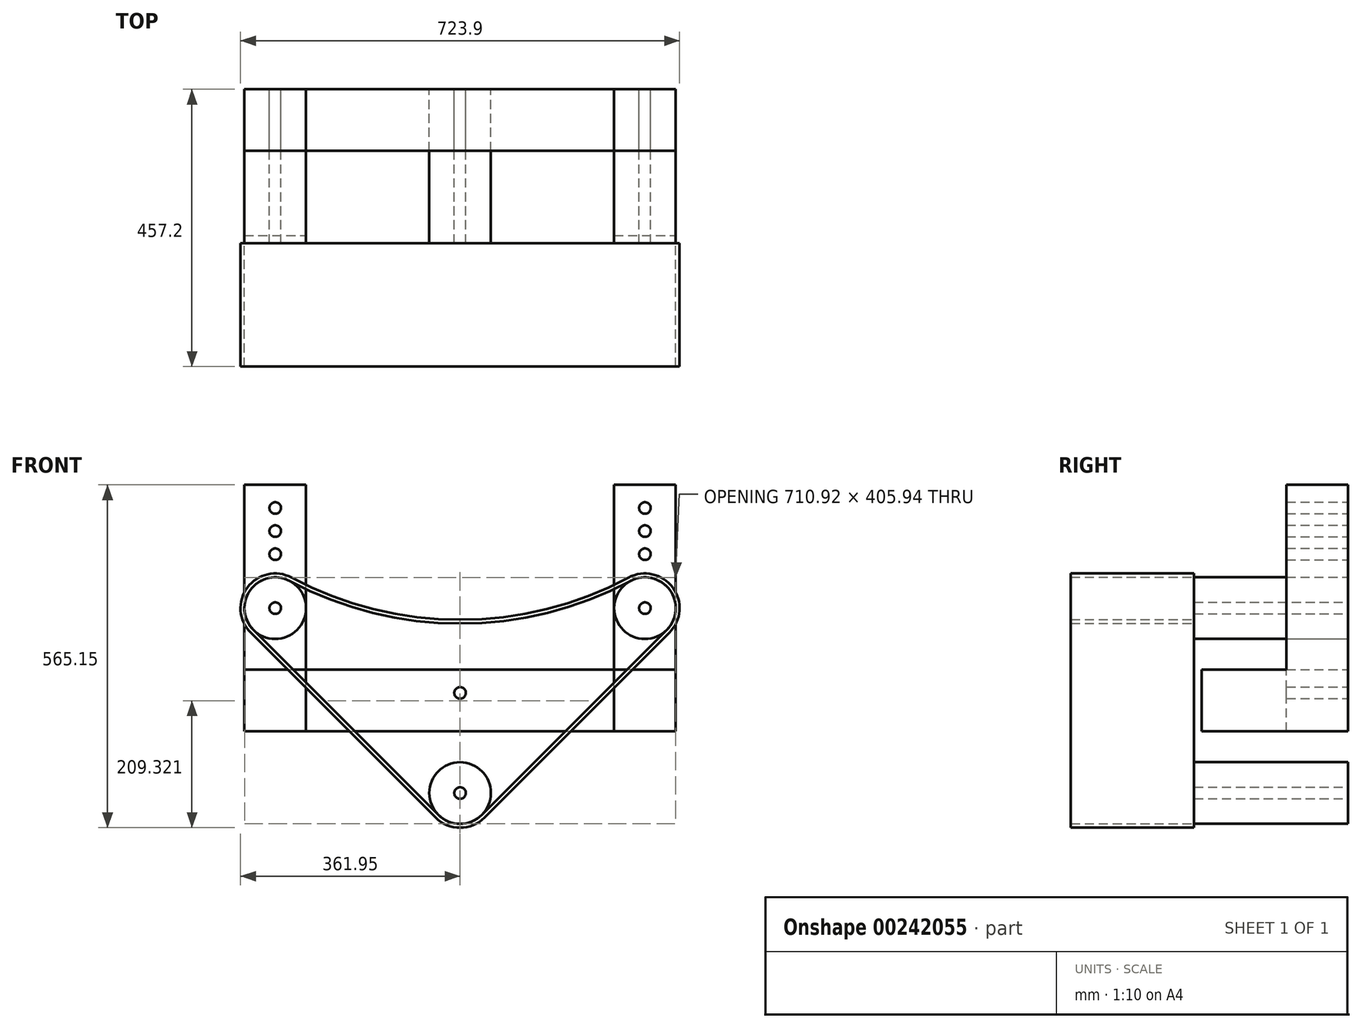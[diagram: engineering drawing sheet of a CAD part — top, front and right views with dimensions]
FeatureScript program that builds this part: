
annotation { "Feature Type Name" : "Feature", "Feature Type Description" : "" }
export const myFeature = defineFeature(function(context is Context, id is Id, definition is map)
    precondition{}
    {
        {
            var Q0;
            Q0=qCreatedBy(makeId("Front.planeOp"),FACE);
            var sketch = newSketch(context, id + "F0", { "sketchPlane" : qUnion([Q0])});
            skCircle(sketch, "E0", {"center": v(-304.8, 0) * mm, "radius": 50.8 * mm});
            skCircle(sketch, "E1", {"center": v(304.8, 0) * mm, "radius": 50.8 * mm});
            skCircle(sketch, "E2", {"center": v(0, -304.8) * mm, "radius": 50.8 * mm});
            skCircle(sketch, "E3", {"center": v(-304.8, 0) * mm, "radius": 9.53 * mm});
            skCircle(sketch, "E4", {"center": v(0, -304.8) * mm, "radius": 9.53 * mm});
            skCircle(sketch, "E5", {"center": v(304.8, 0) * mm, "radius": 9.53 * mm});
            skSolve(sketch);
        }
        {
            var Q0;
            Q0=makeQuery(id+"F0.imprint","IMPRINT",FACE,{"disambiguationData":[TD([[makeQuery(id+"F0.imprint","IMPRINT",EDGE,{"derivedFrom":sQuery(id+"F0.wireOp",EDGE,"E0")}),1.0]])]});
            var Q1;
            Q1=makeQuery(id+"F0.imprint","IMPRINT",FACE,{"disambiguationData":[TD([[makeQuery(id+"F0.imprint","IMPRINT",EDGE,{"derivedFrom":sQuery(id+"F0.wireOp",EDGE,"E1")}),1.0]])]});
            var Q2;
            Q2=makeQuery(id+"F0.imprint","IMPRINT",FACE,{"disambiguationData":[TD([[makeQuery(id+"F0.imprint","IMPRINT",EDGE,{"derivedFrom":sQuery(id+"F0.wireOp",EDGE,"E2")}),1.0]])]});
            extrude(context, id + "F1", {"entities" : qUnion([Q0, Q1, Q2]), "depth" : 254 * mm});
        }
        {
            var Q0;
            Q0=qCreatedBy(makeId("Front.planeOp"),FACE);
            var sketch = newSketch(context, id + "F2", { "sketchPlane" : qUnion([Q0])});
            skLineSegment(sketch, "E6.top", {"start": v(-287.87, 203.2) * mm, "end": v(-321.73, 203.2) * mm});
            skPoint(sketch, "E6.middle", {"position": v(-321.73, 0) * mm});
            skLineSegment(sketch, "E7.left", {"start": v(50.8, -203.2) * mm, "end": v(50.8, -203.2) * mm});
            skLineSegment(sketch, "E7.right", {"start": v(-50.8, -203.2) * mm, "end": v(-50.8, -203.2) * mm});
            skPoint(sketch, "E7.middle", {"position": v(0, -50.8) * mm});
            skLineSegment(sketch, "E8.top", {"start": v(355.6, 203.2) * mm, "end": v(254, 203.2) * mm});
            skPoint(sketch, "E8.middle", {"position": v(304.8, 0) * mm});
            skLineSegment(sketch, "E9", {"start": v(0, -101.6) * mm, "end": v(0, -101.6) * mm});
            skLineSegment(sketch, "E10", {"start": v(304.8, 203.2) * mm, "end": v(304.8, -203.2) * mm, "construction": true});
            skLineSegment(sketch, "E11", {"start": v(-304.8, 203.2) * mm, "end": v(-304.8, -406.4) * mm, "construction": true});
            skCircle(sketch, "E12", {"center": v(-304.8, 165.1) * mm, "radius": 9.53 * mm});
            skCircle(sketch, "E13", {"center": v(304.8, 165.1) * mm, "radius": 9.53 * mm});
            skCircle(sketch, "E14", {"center": v(0, -139.7) * mm, "radius": 9.53 * mm});
            skLineSegment(sketch, "E15.bottom", {"start": v(-355.6, -203.2) * mm, "end": v(355.6, -203.2) * mm});
            skCircle(sketch, "E16.0.1.0", {"center": v(-304.8, 127) * mm, "radius": 9.53 * mm});
            skCircle(sketch, "E16.0.1.1", {"center": v(304.8, 127) * mm, "radius": 9.53 * mm});
            skCircle(sketch, "E16.0.2.0", {"center": v(-304.8, 88.9) * mm, "radius": 9.53 * mm});
            skCircle(sketch, "E16.0.2.1", {"center": v(304.8, 88.9) * mm, "radius": 9.53 * mm});
            skLineSegment(sketch, "E16.direction1", {"start": v(-304.8, 165.1) * mm, "end": v(-279.4, 165.1) * mm, "construction": true});
            skLineSegment(sketch, "E16.direction2", {"start": v(-304.8, 165.1) * mm, "end": v(-304.8, 127) * mm, "construction": true});
            skLineSegment(sketch, "E17", {"start": v(-254, -101.6) * mm, "end": v(254, -101.6) * mm});
            skLineSegment(sketch, "E18", {"start": v(-355.6, -203.2) * mm, "end": v(-355.6, 203.2) * mm});
            skPoint(sketch, "E19.orphan", {"position": v(254, 203.2) * mm});
            skLineSegment(sketch, "E20", {"start": v(355.6, 203.2) * mm, "end": v(355.6, -203.2) * mm});
            skLineSegment(sketch, "E21", {"start": v(254, 203.2) * mm, "end": v(254, -101.6) * mm});
            skLineSegment(sketch, "E22", {"start": v(-254, -101.6) * mm, "end": v(-254, 203.2) * mm});
            skLineSegment(sketch, "E23.trimOffspring", {"start": v(-254, 203.2) * mm, "end": v(-355.6, 203.2) * mm});
            skSolve(sketch);
        }
        {
            var Q0;
            Q0=makeQuery(id+"F2.imprint","IMPRINT",FACE,{"disambiguationData":[TD([[makeQuery(id+"F2.imprint","IMPRINT",EDGE,{"derivedFrom":sQuery(id+"F2.wireOp",EDGE,"E6.top")}),1.0]])]});
            var Q1;
            Q1=makeQuery(id+"F2.imprint","IMPRINT",FACE,{"disambiguationData":[TD([[makeQuery(id+"F2.imprint","IMPRINT",EDGE,{"derivedFrom":sQuery(id+"F2.wireOp",EDGE,"E8.top")}),1.0]])]});
            extrude(context, id + "F3", {"entities" : qUnion([Q0, Q1]), "depth" : 101.6 * mm});
        }
        {
            var Q0;
            Q0=makeQuery(id+"F1.opExtrude","CAP_FACE",FACE,{"disambiguationData":[OSD([sQuery(id+"F0.wireOp",EDGE,"E0"),sQuery(id+"F0.wireOp",EDGE,"E3")])],"isStart":false});
            var sketch = newSketch(context, id + "F4", { "sketchPlane" : qUnion([Q0])});
            skArc(sketch, "E24.0", {"start": v(-280.88, 44.82) * mm, "mid": v(-345.61, 30.25) * mm, "end": v(-340.72, -35.92) * mm});
            skArc(sketch, "E25.0", {"start": v(340.72, -35.92) * mm, "mid": v(345.61, 30.25) * mm, "end": v(280.88, 44.82) * mm});
            skArc(sketch, "E26.0", {"start": v(-35.92, -340.72) * mm, "mid": v(0, -355.6) * mm, "end": v(35.92, -340.72) * mm});
            skLineSegment(sketch, "E27", {"start": v(-340.72, -35.92) * mm, "end": v(-35.92, -340.72) * mm});
            skLineSegment(sketch, "E28", {"start": v(35.92, -340.72) * mm, "end": v(340.72, -35.92) * mm});
            skArc(sketch, "E29", {"start": v(-280.88, 44.82) * mm, "mid": v(0, -25.45) * mm, "end": v(280.88, 44.82) * mm});
            skPoint(sketch, "E29.first.point", {"position": v(-280.88, 44.82) * mm});
            skPoint(sketch, "E29.second.point", {"position": v(280.88, 44.82) * mm});
            skPoint(sketch, "E29.third.point", {"position": v(0, -25.45) * mm});
            skArc(sketch, "E30.0", {"start": v(-277.89, 50.42) * mm, "mid": v(-350.71, 34.03) * mm, "end": v(-345.21, -40.41) * mm});
            skArc(sketch, "E30.1", {"start": v(345.21, -40.41) * mm, "mid": v(350.71, 34.03) * mm, "end": v(277.89, 50.42) * mm});
            skLineSegment(sketch, "E30.2", {"start": v(40.41, -345.21) * mm, "end": v(345.21, -40.41) * mm});
            skArc(sketch, "E30.3", {"start": v(-277.89, 50.42) * mm, "mid": v(0, -19.1) * mm, "end": v(277.89, 50.42) * mm});
            skArc(sketch, "E30.4", {"start": v(-40.41, -345.21) * mm, "mid": v(0, -361.95) * mm, "end": v(40.41, -345.21) * mm});
            skLineSegment(sketch, "E30.5", {"start": v(-345.21, -40.41) * mm, "end": v(-40.41, -345.21) * mm});
            skSolve(sketch);
        }
        {
            var Q0;
            Q0=makeQuery(id+"F4.imprint","IMPRINT",FACE,{"disambiguationData":[TD([[makeQuery(id+"F4.imprint","IMPRINT",EDGE,{"derivedFrom":sQuery(id+"F4.wireOp",EDGE,"E24.0")}),-1.0]])]});
            extrude(context, id + "F5", {"entities" : qUnion([Q0]), "depth" : 203.2 * mm});
        }
        {
            var Q0;
            Q0=makeQuery(id+"F3.opExtrude","CAP_FACE",FACE,{"disambiguationData":[OSD([sQuery(id+"F2.wireOp",EDGE,"E6.top"),sQuery(id+"F2.wireOp",EDGE,"E6.left"),sQuery(id+"F2.wireOp",EDGE,"E6.right"),sQuery(id+"F2.wireOp",EDGE,"E7.top"),sQuery(id+"F2.wireOp",EDGE,"E7.left"),sQuery(id+"F2.wireOp",EDGE,"E7.right"),sQuery(id+"F2.wireOp",EDGE,"E8.top"),sQuery(id+"F2.wireOp",EDGE,"E8.left"),sQuery(id+"F2.wireOp",EDGE,"E8.right"),sQuery(id+"F2.wireOp",EDGE,"E12"),sQuery(id+"F2.wireOp",EDGE,"E13"),sQuery(id+"F2.wireOp",EDGE,"E14"),sQuery(id+"F2.wireOp",EDGE,"E15.bottom"),sQuery(id+"F2.wireOp",EDGE,"E15.left"),sQuery(id+"F2.wireOp",EDGE,"E15.right"),sQuery(id+"F2.wireOp",EDGE,"b9e34c71-d612-4d8c-a427-d50a609893d0.trimOffspring"),sQuery(id+"F2.wireOp",EDGE,"4e111e45-a26a-4544-b2be-adcc2ee35202.trimOffspring")])],"isStart":false});
            var sketch = newSketch(context, id + "F6", { "sketchPlane" : qUnion([Q0])});
            skLineSegment(sketch, "E31.bottom", {"start": v(-355.6, -203.2) * mm, "end": v(-254, -203.2) * mm});
            skLineSegment(sketch, "E31.top", {"start": v(-355.6, -101.6) * mm, "end": v(-254, -101.6) * mm});
            skLineSegment(sketch, "E31.left", {"start": v(-355.6, -203.2) * mm, "end": v(-355.6, -101.6) * mm});
            skLineSegment(sketch, "E31.right", {"start": v(-254, -203.2) * mm, "end": v(-254, -101.6) * mm});
            skLineSegment(sketch, "E32.bottom", {"start": v(355.6, -203.2) * mm, "end": v(254, -203.2) * mm});
            skLineSegment(sketch, "E32.top", {"start": v(355.6, -101.6) * mm, "end": v(254, -101.6) * mm});
            skLineSegment(sketch, "E32.left", {"start": v(355.6, -203.2) * mm, "end": v(355.6, -101.6) * mm});
            skLineSegment(sketch, "E32.right", {"start": v(254, -203.2) * mm, "end": v(254, -101.6) * mm});
            skSolve(sketch);
        }
        {
            var Q0;
            Q0=makeQuery(id+"F6.imprint","IMPRINT",FACE,{"disambiguationData":[TD([[makeQuery(id+"F6.imprint","IMPRINT",EDGE,{"derivedFrom":sQuery(id+"F6.wireOp",EDGE,"E31.bottom")}),1.0]])]});
            var Q1;
            Q1=makeQuery(id+"F6.imprint","IMPRINT",FACE,{"disambiguationData":[TD([[makeQuery(id+"F6.imprint","IMPRINT",EDGE,{"derivedFrom":sQuery(id+"F6.wireOp",EDGE,"PoW8fMG7-Sfxo-Lf8g-mYl7-Ds3I2miW1XXC.bottom")}),1.0]])]});
            var Q2;
            Q2=makeQuery(id+"F6.imprint","IMPRINT",FACE,{"disambiguationData":[TD([[makeQuery(id+"F6.imprint","IMPRINT",EDGE,{"derivedFrom":sQuery(id+"F6.wireOp",EDGE,"E32.bottom")}),1.0]])]});
            extrude(context, id + "F7", {"entities" : qUnion([Q0, Q1, Q2]), "operationType" : NewBodyOperationType.ADD, "depth" : 139.7 * mm});
        }
    });
